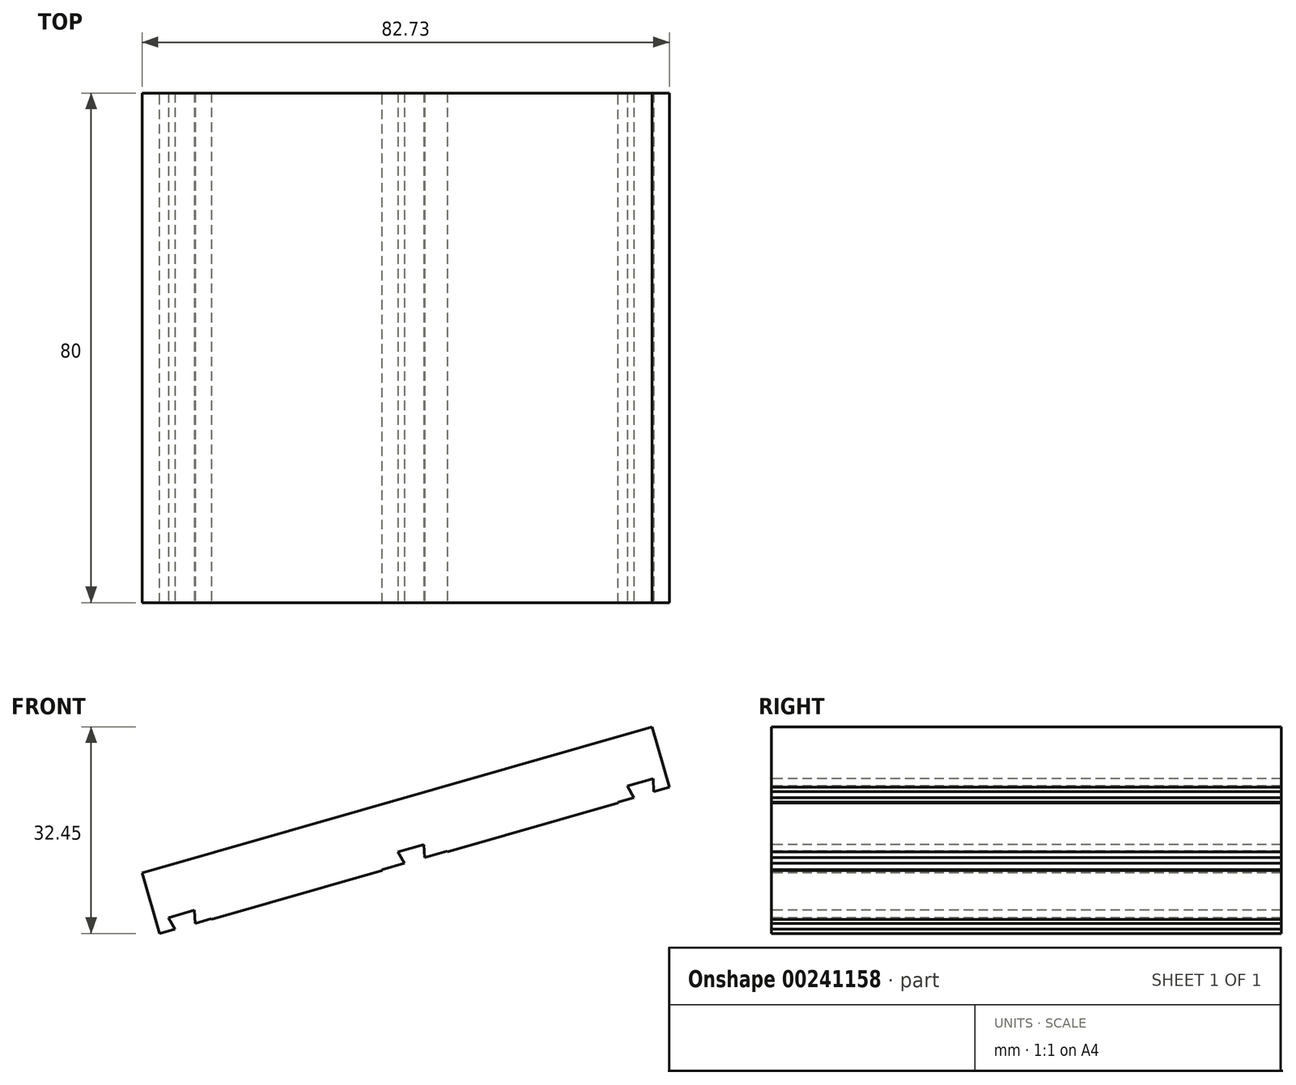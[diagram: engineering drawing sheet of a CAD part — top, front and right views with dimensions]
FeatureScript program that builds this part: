
annotation { "Feature Type Name" : "Feature", "Feature Type Description" : "" }
export const myFeature = defineFeature(function(context is Context, id is Id, definition is map)
    precondition{}
    {
        {
            var Q0;
            Q0=qCreatedBy(makeId("Top.planeOp"),FACE);
            var sketch = newSketch(context, id + "F0", { "sketchPlane" : qUnion([Q0])});
            skLineSegment(sketch, "E0.bottom", {"start": v(-40, -40) * mm, "end": v(40, -40) * mm});
            skLineSegment(sketch, "E0.top", {"start": v(-40, 40) * mm, "end": v(40, 40) * mm});
            skLineSegment(sketch, "E0.left", {"start": v(-40, -40) * mm, "end": v(-40, 40) * mm});
            skLineSegment(sketch, "E0.right", {"start": v(40, -40) * mm, "end": v(40, 40) * mm});
            skLineSegment(sketch, "E1", {"start": v(0, 40) * mm, "end": v(0, -40) * mm, "construction": true});
            skLineSegment(sketch, "E2", {"start": v(-40, 0) * mm, "end": v(40, 0) * mm, "construction": true});
            skPoint(sketch, "E3", {"position": v(0, 0) * mm});
            skSolve(sketch);
        }
        {
            var Q0;
            Q0=makeQuery(id+"F0.imprint","IMPRINT",FACE,{"disambiguationData":[TD([[makeQuery(id+"F0.imprint","IMPRINT",EDGE,{"derivedFrom":sQuery(id+"F0.wireOp",EDGE,"E0.bottom")}),1.0]])]});
            extrude(context, id + "F1", {"entities" : qUnion([Q0]), "depth" : 10 * mm});
        }
        {
            var Q0;
            Q0=makeQuery(id+"F1.opExtrude","CAP_FACE",FACE,{"disambiguationData":[OSD([sQuery(id+"F0.wireOp",EDGE,"E0.bottom"),sQuery(id+"F0.wireOp",EDGE,"E0.top"),sQuery(id+"F0.wireOp",EDGE,"E0.left"),sQuery(id+"F0.wireOp",EDGE,"E0.right")])],"isStart":false});
            var sketch = newSketch(context, id + "F2", { "sketchPlane" : qUnion([Q0])});
            skLineSegment(sketch, "E4", {"start": v(-40, 0) * mm, "end": v(40, 0) * mm, "construction": true});
            skLineSegment(sketch, "E5", {"start": v(0, 40) * mm, "end": v(0, -40) * mm, "construction": true});
            skLineSegment(sketch, "E6", {"start": v(-26.75, 25) * mm, "end": v(26.75, 25) * mm, "construction": true});
            skLineSegment(sketch, "E7", {"start": v(-26.75, 25) * mm, "end": v(-26.75, -25) * mm, "construction": true});
            skPoint(sketch, "E8", {"position": v(-26.75, 0) * mm});
            skArc(sketch, "E9.0.startCap", {"start": v(-26.75, 21.75) * mm, "mid": v(-30, 25) * mm, "end": v(-26.75, 28.25) * mm});
            skArc(sketch, "E9.0.endCap", {"start": v(26.75, 28.25) * mm, "mid": v(30, 25) * mm, "end": v(26.75, 21.75) * mm});
            skLineSegment(sketch, "E9.0.left", {"start": v(-26.75, 28.25) * mm, "end": v(26.75, 28.25) * mm});
            skLineSegment(sketch, "E9.0.right", {"start": v(-26.75, 21.75) * mm, "end": v(26.75, 21.75) * mm});
            skPoint(sketch, "E10", {"position": v(0, 25) * mm});
            skLineSegment(sketch, "E11.0.1.0", {"start": v(-26.75, 3.25) * mm, "end": v(26.75, 3.25) * mm});
            skArc(sketch, "E11.0.1.1", {"start": v(26.75, 3.25) * mm, "mid": v(30, 0) * mm, "end": v(26.75, -3.25) * mm});
            skArc(sketch, "E11.0.1.2", {"start": v(-26.75, -3.25) * mm, "mid": v(-30, 0) * mm, "end": v(-26.75, 3.25) * mm});
            skLineSegment(sketch, "E11.0.1.3", {"start": v(-26.75, 0) * mm, "end": v(26.75, 0) * mm, "construction": true});
            skPoint(sketch, "E11.0.1.4", {"position": v(0, 0) * mm});
            skLineSegment(sketch, "E11.0.1.5", {"start": v(-26.75, -3.25) * mm, "end": v(26.75, -3.25) * mm});
            skLineSegment(sketch, "E11.0.2.0", {"start": v(-26.75, -21.75) * mm, "end": v(26.75, -21.75) * mm});
            skArc(sketch, "E11.0.2.1", {"start": v(26.75, -21.75) * mm, "mid": v(30, -25) * mm, "end": v(26.75, -28.25) * mm});
            skArc(sketch, "E11.0.2.2", {"start": v(-26.75, -28.25) * mm, "mid": v(-30, -25) * mm, "end": v(-26.75, -21.75) * mm});
            skLineSegment(sketch, "E11.0.2.3", {"start": v(-26.75, -25) * mm, "end": v(26.75, -25) * mm, "construction": true});
            skPoint(sketch, "E11.0.2.4", {"position": v(0, -25) * mm});
            skLineSegment(sketch, "E11.0.2.5", {"start": v(-26.75, -28.25) * mm, "end": v(26.75, -28.25) * mm});
            skLineSegment(sketch, "E11.direction1", {"start": v(-26.75, 21.75) * mm, "end": v(98.6, 15.7) * mm, "construction": true});
            skLineSegment(sketch, "E11.direction2", {"start": v(-26.75, 21.75) * mm, "end": v(-26.75, -3.25) * mm, "construction": true});
            skSolve(sketch);
        }
        {
            var Q0;
            Q0=qSketchRegion(id+"F2",true);
            extrude(context, id + "F3", {"entities" : qUnion([Q0]), "operationType" : NewBodyOperationType.REMOVE, "endBound" : BoundingType.UP_TO_NEXT, "oppositeDirection" : true, "depth" : 25 * mm});
        }
        {
            var Q0;
            Q0=makeQuery(id+"F1.opExtrude","CAP_FACE",FACE,{"disambiguationData":[OSD([sQuery(id+"F0.wireOp",EDGE,"E0.bottom"),sQuery(id+"F0.wireOp",EDGE,"E0.top"),sQuery(id+"F0.wireOp",EDGE,"E0.left"),sQuery(id+"F0.wireOp",EDGE,"E0.right")])],"isStart":false});
            var sketch = newSketch(context, id + "F4", { "sketchPlane" : qUnion([Q0])});
            skLineSegment(sketch, "E12.bottom", {"start": v(-40, 40) * mm, "end": v(-32, 40) * mm});
            skLineSegment(sketch, "E12.top", {"start": v(-40, -40) * mm, "end": v(-32, -40) * mm});
            skLineSegment(sketch, "E12.left", {"start": v(-40, -40) * mm, "end": v(-40, 40) * mm});
            skLineSegment(sketch, "E12.right", {"start": v(-32, -40) * mm, "end": v(-32, 40) * mm});
            skLineSegment(sketch, "E13", {"start": v(-40, 0) * mm, "end": v(40, 0) * mm, "construction": true});
            skPoint(sketch, "E14", {"position": v(40, 0) * mm});
            skLineSegment(sketch, "E15.bottom", {"start": v(5, -40) * mm, "end": v(-5, -40) * mm});
            skLineSegment(sketch, "E15.top", {"start": v(5, -34) * mm, "end": v(-5, -34) * mm});
            skLineSegment(sketch, "E15.left", {"start": v(5, -40) * mm, "end": v(5, -34) * mm});
            skLineSegment(sketch, "E15.right", {"start": v(-5, -40) * mm, "end": v(-5, -34) * mm});
            skPoint(sketch, "E16", {"position": v(0, -40) * mm});
            skLineSegment(sketch, "E17.bottom", {"start": v(32, -28) * mm, "end": v(40, -28) * mm});
            skLineSegment(sketch, "E17.top", {"start": v(32, -40) * mm, "end": v(40, -40) * mm});
            skLineSegment(sketch, "E17.left", {"start": v(32, -28) * mm, "end": v(32, -40) * mm});
            skLineSegment(sketch, "E17.right", {"start": v(40, -28) * mm, "end": v(40, -40) * mm});
            skSolve(sketch);
        }
        {
            var Q0;
            Q0 = qSketchRegion(id + "F4", true);
            extrude(context, id + "F5", {"entities" : qUnion([Q0]), "operationType" : NewBodyOperationType.ADD, "depth" : 80 * mm});
        }
        {
            var Q0;
            Q0=makeQuery(id+"F5.boolean.opBoolean","MERGE",FACE,{"derivedFrom":[makeQuery(id+"F1.opExtrude","SWEPT_FACE",FACE,{"disambiguationData":[OSD([sQuery(id+"F0.wireOp",EDGE,"E0.bottom")])]}),makeQuery(id+"F5.opExtrude","SWEPT_FACE",FACE,{"disambiguationData":[OSD([sQuery(id+"F4.wireOp",EDGE,"E12.top")])]}),makeQuery(id+"F5.opExtrude","SWEPT_FACE",FACE,{"disambiguationData":[OSD([sQuery(id+"F4.wireOp",EDGE,"E15.bottom")])]}),makeQuery(id+"F5.opExtrude","SWEPT_FACE",FACE,{"disambiguationData":[OSD([sQuery(id+"F4.wireOp",EDGE,"E17.top")])]})]});
            var sketch = newSketch(context, id + "F6", { "sketchPlane" : qUnion([Q0])});
            skLineSegment(sketch, "E18", {"start": v(62.9, 40.5) * mm, "end": v(62.9, 116.62) * mm});
            skLineSegment(sketch, "E19", {"start": v(62.9, 116.62) * mm, "end": v(-43.24, 116.62) * mm});
            skLineSegment(sketch, "E20", {"start": v(-43.24, 116.62) * mm, "end": v(-43.49, 10) * mm});
            skLineSegment(sketch, "E21", {"start": v(-43.49, 10) * mm, "end": v(63.84, 10) * mm, "construction": true});
            skLineSegment(sketch, "E22", {"start": v(-43.49, 10) * mm, "end": v(-40, 11) * mm});
            skLineSegment(sketch, "E23", {"start": v(-37.44, 11.73) * mm, "end": v(-38.47, 13.52) * mm});
            skLineSegment(sketch, "E24", {"start": v(-34.63, 14.62) * mm, "end": v(-38.47, 13.52) * mm});
            skLineSegment(sketch, "E25", {"start": v(-34.63, 14.62) * mm, "end": v(-34.56, 12.56) * mm});
            skLineSegment(sketch, "E26", {"start": v(-36.55, 14.07) * mm, "end": v(-36, 12.15) * mm, "construction": true});
            skLineSegment(sketch, "E27", {"start": v(-34.56, 12.56) * mm, "end": v(-32, 13.3) * mm});
            skLineSegment(sketch, "E28", {"start": v(-40, 11) * mm, "end": v(-37.44, 11.73) * mm});
            skLineSegment(sketch, "E29", {"start": v(-37.44, 11.73) * mm, "end": v(-36, 12.15) * mm, "construction": true});
            skLineSegment(sketch, "E30", {"start": v(-34.56, 12.56) * mm, "end": v(-36, 12.15) * mm, "construction": true});
            skLineSegment(sketch, "E31", {"start": v(-32, 13.3) * mm, "end": v(-5, 21.04) * mm});
            skLineSegment(sketch, "E32", {"start": v(-1.44, 22.06) * mm, "end": v(-2.47, 23.84) * mm});
            skLineSegment(sketch, "E33", {"start": v(1.37, 24.94) * mm, "end": v(-2.47, 23.84) * mm});
            skLineSegment(sketch, "E34", {"start": v(1.37, 24.94) * mm, "end": v(1.44, 22.88) * mm});
            skLineSegment(sketch, "E35", {"start": v(-0.55, 24.4) * mm, "end": v(0, 22.47) * mm, "construction": true});
            skLineSegment(sketch, "E36", {"start": v(1.44, 22.88) * mm, "end": v(5, 23.9) * mm});
            skLineSegment(sketch, "E37", {"start": v(-5, 21.04) * mm, "end": v(-1.44, 22.06) * mm});
            skLineSegment(sketch, "E38", {"start": v(-1.44, 22.06) * mm, "end": v(0, 22.47) * mm, "construction": true});
            skLineSegment(sketch, "E39", {"start": v(1.44, 22.88) * mm, "end": v(0, 22.47) * mm, "construction": true});
            skLineSegment(sketch, "E40", {"start": v(5, 23.9) * mm, "end": v(32, 31.65) * mm});
            skLineSegment(sketch, "E41", {"start": v(34.56, 32.38) * mm, "end": v(33.53, 34.16) * mm});
            skLineSegment(sketch, "E42", {"start": v(37.37, 35.27) * mm, "end": v(33.53, 34.16) * mm});
            skLineSegment(sketch, "E43", {"start": v(37.37, 35.27) * mm, "end": v(37.44, 33.2) * mm});
            skLineSegment(sketch, "E44", {"start": v(35.45, 34.72) * mm, "end": v(36, 32.8) * mm, "construction": true});
            skLineSegment(sketch, "E45", {"start": v(37.44, 33.2) * mm, "end": v(40, 33.94) * mm});
            skLineSegment(sketch, "E46", {"start": v(32, 31.65) * mm, "end": v(34.56, 32.38) * mm});
            skLineSegment(sketch, "E47", {"start": v(34.56, 32.38) * mm, "end": v(36, 32.8) * mm, "construction": true});
            skLineSegment(sketch, "E48", {"start": v(37.44, 33.2) * mm, "end": v(36, 32.8) * mm, "construction": true});
            skLineSegment(sketch, "E49", {"start": v(40, 33.94) * mm, "end": v(62.9, 40.5) * mm});
            skSolve(sketch);
        }
        {
            var Q0;
            Q0 = qSketchRegion(id + "F6", true);
            extrude(context, id + "F7", {"entities" : qUnion([Q0]), "operationType" : NewBodyOperationType.REMOVE, "endBound" : BoundingType.THROUGH_ALL, "oppositeDirection" : true, "depth" : 25 * mm});
        }
        {
            var Q0;
            Q0=makeQuery(id+"F1.opExtrude","SWEPT_BODY",BODY,{"disambiguationData":[OSD([sQuery(id+"F0.wireOp",EDGE,"E0.bottom"),sQuery(id+"F0.wireOp",EDGE,"E0.top"),sQuery(id+"F0.wireOp",EDGE,"E0.left"),sQuery(id+"F0.wireOp",EDGE,"E0.right")])]});
            var Q1;
            Q1=qCreatedBy(makeId("Front.planeOp"),FACE);
            mirror(context, id + "F8", {"operationType" : NewBodyOperationType.ADD, "entities" : qUnion([Q0]), "mirrorPlane" : qUnion([Q1])});
        }
        {
            var Q0;
            Q0=makeQuery(id+"F7.boolean.opBoolean","COPY",FACE,{"disambiguationData":[TD([makeQuery(id+"F1.opExtrude","SWEPT_FACE",FACE,{"disambiguationData":[OSD([sQuery(id+"F0.wireOp",EDGE,"E0.top")])]})])],"derivedFrom":makeQuery(id+"F7.opExtrude","SWEPT_FACE",FACE,{"disambiguationData":[OSD([sQuery(id+"F6.wireOp",EDGE,"E27"),sQuery(id+"F6.wireOp",EDGE,"E31"),sQuery(id+"F6.wireOp",EDGE,"E37")])]})});
            cPlane(context, id + "F9", {"entities" : qUnion([Q0]), "cplaneType" : CPlaneType.OFFSET, "offset" : 10 * mm, "width" : 150 * mm, "height" : 150 * mm});
        }
        {
            var Q0;
            Q0=qCreatedBy(id+"F9.planeOp",FACE);
            var sketch = newSketch(context, id + "F10", { "sketchPlane" : qUnion([Q0])});
            skLineSegment(sketch, "E50.0", {"start": v(-35.42, 40) * mm, "end": v(-35.42, -40) * mm});
            skLineSegment(sketch, "E50.1", {"start": v(-32.76, 40) * mm, "end": v(-35.42, 40) * mm, "construction": true});
            skLineSegment(sketch, "E50.2", {"start": v(45.14, -40) * mm, "end": v(47.8, -40) * mm, "construction": true});
            skLineSegment(sketch, "E50.3", {"start": v(47.8, -28) * mm, "end": v(47.8, -40) * mm, "construction": true});
            skLineSegment(sketch, "E51.bottom", {"start": v(-35.42, 40) * mm, "end": v(47.8, 40) * mm});
            skLineSegment(sketch, "E51.top", {"start": v(-35.42, -40) * mm, "end": v(47.8, -40) * mm});
            skLineSegment(sketch, "E51.left", {"start": v(-35.42, 40) * mm, "end": v(-35.42, -40) * mm, "construction": true});
            skLineSegment(sketch, "E51.right", {"start": v(47.8, 40) * mm, "end": v(47.8, -40) * mm});
            skSolve(sketch);
        }
        {
            var Q0;
            Q0 = qSketchRegion(id + "F10", true);
            var Q1;
            Q1=makeQuery(id+"F7.boolean.opBoolean","COPY",FACE,{"derivedFrom":makeQuery(id+"F7.opExtrude","SWEPT_FACE",FACE,{"disambiguationData":[OSD([sQuery(id+"F6.wireOp",EDGE,"E45"),sQuery(id+"F6.wireOp",EDGE,"E49")])]})});
            var Q2;
            Q2=makeQuery(id+"F1.opExtrude","SWEPT_BODY",BODY,{"disambiguationData":[OSD([sQuery(id+"F0.wireOp",EDGE,"E0.bottom"),sQuery(id+"F0.wireOp",EDGE,"E0.top"),sQuery(id+"F0.wireOp",EDGE,"E0.left"),sQuery(id+"F0.wireOp",EDGE,"E0.right")])]});
            extrude(context, id + "F11", {"entities" : qUnion([Q0]), "endBound" : BoundingType.UP_TO_SURFACE, "oppositeDirection" : true, "endBoundEntityFace" : qUnion([Q1]), "endBoundEntityBody" : qUnion([Q2]), "depth" : 25 * mm});
        }
        {
            var Q0;
            Q0=makeQuery(id+"F11.opExtrude","SWEPT_FACE",FACE,{"disambiguationData":[OSD([sQuery(id+"F10.wireOp",EDGE,"E51.top")])]});
            var sketch = newSketch(context, id + "F12", { "sketchPlane" : qUnion([Q0])});
            skLineSegment(sketch, "E52.0.0", {"start": v(32, 31.65) * mm, "end": v(32, 10) * mm, "construction": true});
            skLineSegment(sketch, "E52.0.1", {"start": v(32, 10) * mm, "end": v(5, 10) * mm, "construction": true});
            skLineSegment(sketch, "E52.0.2", {"start": v(5, 10) * mm, "end": v(5, 23.9) * mm, "construction": true});
            skLineSegment(sketch, "E52.0.3", {"start": v(5, 23.9) * mm, "end": v(1.44, 22.88) * mm, "construction": true});
            skLineSegment(sketch, "E52.0.4", {"start": v(1.44, 22.88) * mm, "end": v(1.37, 24.94) * mm, "construction": true});
            skLineSegment(sketch, "E52.0.5", {"start": v(1.37, 24.94) * mm, "end": v(-2.47, 23.84) * mm, "construction": true});
            skLineSegment(sketch, "E52.0.6", {"start": v(-2.47, 23.84) * mm, "end": v(-1.44, 22.06) * mm, "construction": true});
            skLineSegment(sketch, "E52.0.7", {"start": v(-1.44, 22.06) * mm, "end": v(-5, 21.04) * mm, "construction": true});
            skLineSegment(sketch, "E52.0.8", {"start": v(-5, 21.04) * mm, "end": v(-5, 10) * mm, "construction": true});
            skLineSegment(sketch, "E52.0.9", {"start": v(-5, 10) * mm, "end": v(-32, 10) * mm, "construction": true});
            skLineSegment(sketch, "E52.0.10", {"start": v(-32, 10) * mm, "end": v(-32, 13.3) * mm, "construction": true});
            skLineSegment(sketch, "E52.0.11", {"start": v(-32, 13.3) * mm, "end": v(-34.56, 12.56) * mm, "construction": true});
            skLineSegment(sketch, "E52.0.12", {"start": v(-34.56, 12.56) * mm, "end": v(-34.63, 14.62) * mm, "construction": true});
            skLineSegment(sketch, "E52.0.13", {"start": v(-34.63, 14.62) * mm, "end": v(-38.47, 13.52) * mm, "construction": true});
            skLineSegment(sketch, "E52.0.14", {"start": v(-38.47, 13.52) * mm, "end": v(-37.44, 11.73) * mm, "construction": true});
            skLineSegment(sketch, "E52.0.15", {"start": v(-37.44, 11.73) * mm, "end": v(-40, 11) * mm, "construction": true});
            skLineSegment(sketch, "E52.0.16", {"start": v(-40, 11) * mm, "end": v(-40, 0) * mm, "construction": true});
            skLineSegment(sketch, "E52.0.17", {"start": v(-40, 0) * mm, "end": v(40, 0) * mm, "construction": true});
            skLineSegment(sketch, "E52.0.18", {"start": v(40, 0) * mm, "end": v(40, 33.94) * mm, "construction": true});
            skLineSegment(sketch, "E52.0.19", {"start": v(40, 33.94) * mm, "end": v(37.44, 33.2) * mm, "construction": true});
            skLineSegment(sketch, "E52.0.20", {"start": v(37.44, 33.2) * mm, "end": v(37.37, 35.27) * mm, "construction": true});
            skLineSegment(sketch, "E52.0.21", {"start": v(37.37, 35.27) * mm, "end": v(33.53, 34.16) * mm, "construction": true});
            skLineSegment(sketch, "E52.0.22", {"start": v(33.53, 34.16) * mm, "end": v(34.56, 32.38) * mm, "construction": true});
            skLineSegment(sketch, "E52.0.23", {"start": v(34.56, 32.38) * mm, "end": v(32, 31.65) * mm, "construction": true});
            skLineSegment(sketch, "E53.0", {"start": v(-5.1, 21.11) * mm, "end": v(-5.1, 10.1) * mm});
            skLineSegment(sketch, "E53.1", {"start": v(40.1, 34.07) * mm, "end": v(37.54, 33.34) * mm});
            skLineSegment(sketch, "E53.2", {"start": v(40.1, -0.1) * mm, "end": v(40.1, 34.07) * mm});
            skLineSegment(sketch, "E53.3", {"start": v(-40.1, -0.1) * mm, "end": v(40.1, -0.1) * mm});
            skLineSegment(sketch, "E53.4", {"start": v(-40.1, 11.08) * mm, "end": v(-40.1, -0.1) * mm});
            skLineSegment(sketch, "E53.5", {"start": v(-37.6, 11.8) * mm, "end": v(-40.1, 11.08) * mm});
            skLineSegment(sketch, "E53.6", {"start": v(-38.62, 13.58) * mm, "end": v(-37.6, 11.8) * mm});
            skLineSegment(sketch, "E53.7", {"start": v(-31.9, 10.1) * mm, "end": v(-31.9, 13.43) * mm});
            skLineSegment(sketch, "E53.8", {"start": v(-31.9, 13.43) * mm, "end": v(-34.46, 12.7) * mm});
            skLineSegment(sketch, "E53.9", {"start": v(-34.46, 12.7) * mm, "end": v(-34.53, 14.75) * mm});
            skLineSegment(sketch, "E53.10", {"start": v(-34.53, 14.75) * mm, "end": v(-38.62, 13.58) * mm});
            skLineSegment(sketch, "E53.11", {"start": v(37.54, 33.34) * mm, "end": v(37.47, 35.4) * mm});
            skLineSegment(sketch, "E53.12", {"start": v(-5.1, 10.1) * mm, "end": v(-31.9, 10.1) * mm});
            skLineSegment(sketch, "E53.13", {"start": v(37.47, 35.4) * mm, "end": v(33.38, 34.22) * mm});
            skLineSegment(sketch, "E53.14", {"start": v(33.38, 34.22) * mm, "end": v(34.4, 32.44) * mm});
            skLineSegment(sketch, "E53.15", {"start": v(34.4, 32.44) * mm, "end": v(31.9, 31.72) * mm});
            skLineSegment(sketch, "E53.16", {"start": v(31.9, 31.72) * mm, "end": v(31.9, 10.1) * mm});
            skLineSegment(sketch, "E53.17", {"start": v(31.9, 10.1) * mm, "end": v(5.1, 10.1) * mm});
            skLineSegment(sketch, "E53.18", {"start": v(5.1, 10.1) * mm, "end": v(5.1, 24.04) * mm});
            skLineSegment(sketch, "E53.19", {"start": v(5.1, 24.04) * mm, "end": v(1.54, 23.01) * mm});
            skLineSegment(sketch, "E53.20", {"start": v(1.54, 23.01) * mm, "end": v(1.47, 25.08) * mm});
            skLineSegment(sketch, "E53.21", {"start": v(1.47, 25.08) * mm, "end": v(-2.62, 23.9) * mm});
            skLineSegment(sketch, "E53.22", {"start": v(-2.62, 23.9) * mm, "end": v(-1.6, 22.12) * mm});
            skLineSegment(sketch, "E53.23", {"start": v(-1.6, 22.12) * mm, "end": v(-5.1, 21.11) * mm});
            skSolve(sketch);
        }
        {
            var Q0;
            Q0 = qSketchRegion(id + "F12", true);
            extrude(context, id + "F13", {"entities" : qUnion([Q0]), "operationType" : NewBodyOperationType.REMOVE, "endBound" : BoundingType.THROUGH_ALL, "oppositeDirection" : true, "depth" : 25 * mm});
        }
    });
